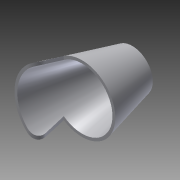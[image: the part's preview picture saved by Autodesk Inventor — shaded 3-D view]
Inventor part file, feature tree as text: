
AUTODESK INVENTOR PART (.ipt)
format: ipt  version: 2015 (Build 190159000, 159)  size: 168,448 bytes
history: native  units: mm
features: sketch x4, extrude x2, revolve x1, shell x1, hole x1, fillet x1, pattern_circular x1
ambient origin geometry x8: Origin, YZ Plane, XZ Plane, XY Plane, X Axis, Y Axis, Z Axis, Center Point
bodies: Body1 (feature_tree)
feature tree (11):
  revolve  "回転1"
  shell  "シェル2"  Thickness=22.5mm
  hole  "穴2"  [1 undecoded]
  extrude  "押し出し6"  Depth=85.0mm
  fillet  "フィレット3"  [1 undecoded]
  extrude  "押し出し7"  Depth=3.0mm
  pattern_circular  "円形状パターン2"  [2 undecoded]
  sketch  "スケッチ8"
  sketch  "スケッチ9"
  sketch  "スケッチ16"
  sketch  "スケッチ17"
note: 4 required parameter values undecoded (feature->parameter linkage not recoverable at this tier; creation-order binding heuristic only, values carry confidence <= 0.55)
